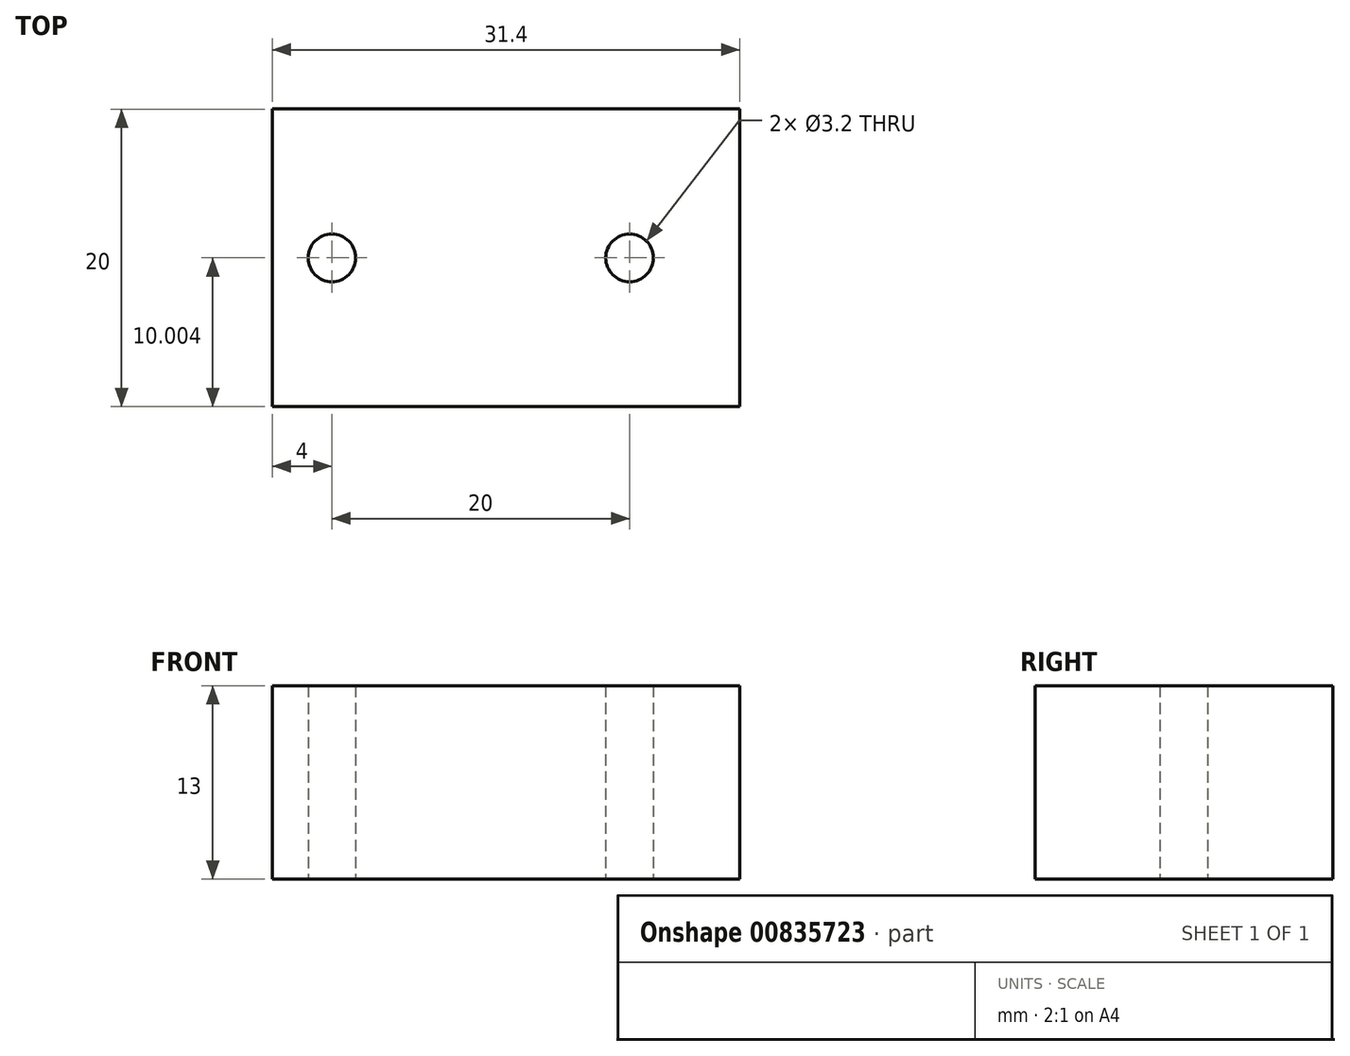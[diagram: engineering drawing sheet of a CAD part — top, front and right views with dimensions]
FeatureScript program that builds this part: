
annotation { "Feature Type Name" : "Feature", "Feature Type Description" : "" }
export const myFeature = defineFeature(function(context is Context, id is Id, definition is map)
    precondition{}
    {
        {
            var Q0;
            Q0=qCreatedBy(makeId("Top.planeOp"),FACE);
            var sketch = newSketch(context, id + "F0", { "sketchPlane" : qUnion([Q0])});
            skCircle(sketch, "E0", {"center": v(-55.34, -19.27) * mm, "radius": 2.05 * mm});
            skCircle(sketch, "E1", {"center": v(-55.34, -66.87) * mm, "radius": 2.05 * mm});
            skCircle(sketch, "E2", {"center": v(-46.19, -43.07) * mm, "radius": 1.6 * mm});
            skCircle(sketch, "E3", {"center": v(-26.19, -43.07) * mm, "radius": 1.6 * mm});
            skCircle(sketch, "E4", {"center": v(-97.34, -33.07) * mm, "radius": 1.59 * mm});
            skCircle(sketch, "E5", {"center": v(-77.34, -33.07) * mm, "radius": 1.59 * mm});
            skCircle(sketch, "E6", {"center": v(-97.34, -53.07) * mm, "radius": 1.59 * mm});
            skCircle(sketch, "E7", {"center": v(-77.34, -53.07) * mm, "radius": 1.59 * mm});
            skLineSegment(sketch, "E8.right", {"start": v(-18.79, -19.07) * mm, "end": v(-18.79, -67.07) * mm});
            skLineSegment(sketch, "E9", {"start": v(-102.38, -19.08) * mm, "end": v(-102.22, -67.08) * mm});
            skLineSegment(sketch, "E10", {"start": v(-97.38, -14.07) * mm, "end": v(-23.79, -14.07) * mm});
            skLineSegment(sketch, "E11", {"start": v(-23.79, -72.07) * mm, "end": v(-97.22, -72.07) * mm});
            skArc(sketch, "E12.filletArc", {"start": v(-97.38, -14.07) * mm, "mid": v(-100.93, -15.54) * mm, "end": v(-102.38, -19.08) * mm});
            skArc(sketch, "E13.filletArc", {"start": v(-18.79, -19.07) * mm, "mid": v(-20.25, -15.53) * mm, "end": v(-23.79, -14.07) * mm});
            skArc(sketch, "E14.filletArc", {"start": v(-23.79, -72.07) * mm, "mid": v(-20.25, -70.6) * mm, "end": v(-18.79, -67.07) * mm});
            skArc(sketch, "E15.filletArc", {"start": v(-102.22, -67.08) * mm, "mid": v(-100.75, -70.6) * mm, "end": v(-97.22, -72.07) * mm});
            skLineSegment(sketch, "E16.bottom", {"start": v(-18.79, -33.07) * mm, "end": v(-50.19, -33.07) * mm});
            skLineSegment(sketch, "E16.top", {"start": v(-18.79, -53.07) * mm, "end": v(-50.19, -53.07) * mm});
            skLineSegment(sketch, "E16.left", {"start": v(-18.79, -33.07) * mm, "end": v(-18.79, -53.07) * mm});
            skLineSegment(sketch, "E16.right", {"start": v(-50.19, -33.07) * mm, "end": v(-50.19, -53.07) * mm});
            skSolve(sketch);
        }
        {
            var Q0;
            Q0=makeQuery(id+"F0.imprint","IMPRINT",FACE,{"disambiguationData":[TD([[makeQuery(id+"F0.imprint","IMPRINT",EDGE,{"derivedFrom":sQuery(id+"F0.wireOp",EDGE,"E2")}),-1.0]])]});
            extrude(context, id + "F1", {"entities" : qUnion([Q0]), "depth" : 13 * mm, "offsetDistance" : 25 * mm});
        }
    });
